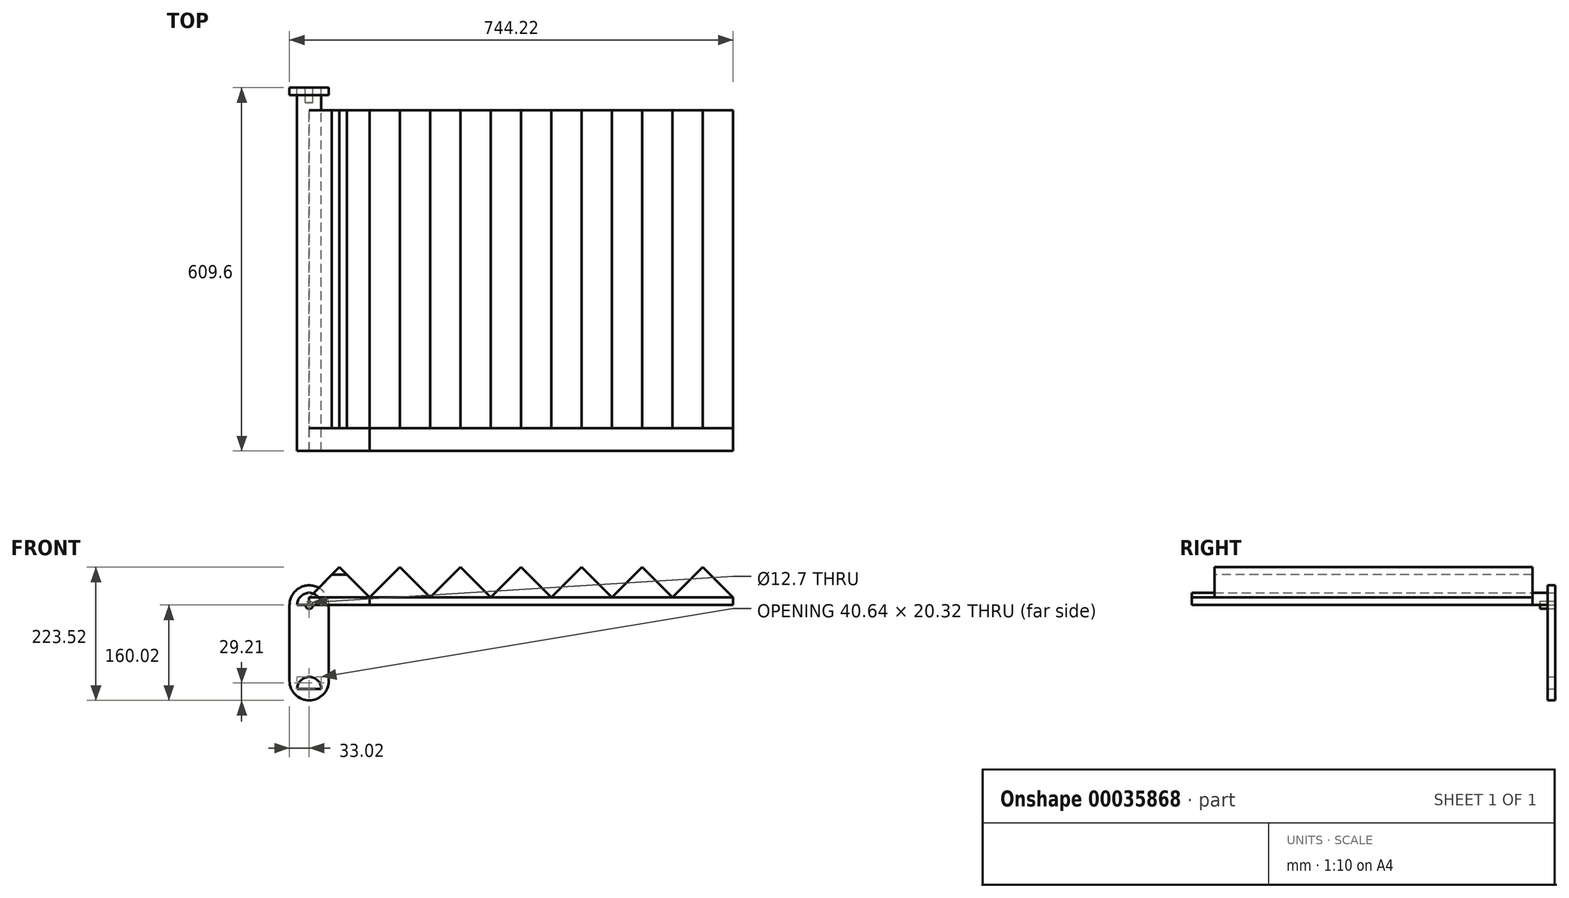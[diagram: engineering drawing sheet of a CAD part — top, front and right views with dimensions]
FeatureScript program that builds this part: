
annotation { "Feature Type Name" : "Feature", "Feature Type Description" : "" }
export const myFeature = defineFeature(function(context is Context, id is Id, definition is map)
    precondition{}
    {
        {
            var Q0;
            Q0=qCreatedBy(makeId("Front.planeOp"),FACE);
            var sketch = newSketch(context, id + "F0", { "sketchPlane" : qUnion([Q0])});
            skLineSegment(sketch, "E0.bottom", {"start": v(0, 0) * mm, "end": v(101.6, 0) * mm});
            skLineSegment(sketch, "E0.top", {"start": v(0, 50.8) * mm, "end": v(101.6, 50.8) * mm});
            skLineSegment(sketch, "E0.left", {"start": v(0, 0) * mm, "end": v(0, 50.8) * mm});
            skLineSegment(sketch, "E0.right", {"start": v(101.6, 0) * mm, "end": v(101.6, 50.8) * mm});
            skSolve(sketch);
        }
        {
            var Q0;
            Q0 = qSketchRegion(id + "F0", true);
            extrude(context, id + "F1", {"entities" : qUnion([Q0]), "depth" : 609.6 * mm});
        }
        {
            var Q0;
            Q0=qCreatedBy(makeId("Front.planeOp"),FACE);
            var sketch = newSketch(context, id + "F2", { "sketchPlane" : qUnion([Q0])});
            skLineSegment(sketch, "E1.bottom", {"start": v(0, 0) * mm, "end": v(711.2, 0) * mm});
            skLineSegment(sketch, "E1.top", {"start": v(0, 63.5) * mm, "end": v(711.2, 63.5) * mm});
            skLineSegment(sketch, "E1.left", {"start": v(0, 0) * mm, "end": v(0, 63.5) * mm});
            skLineSegment(sketch, "E1.right", {"start": v(711.2, 0) * mm, "end": v(711.2, 63.5) * mm});
            skSolve(sketch);
        }
        {
            var Q0;
            Q0 = qSketchRegion(id + "F2", true);
            extrude(context, id + "F3", {"entities" : qUnion([Q0]), "depth" : 609.6 * mm});
        }
        {
            var Q0;
            Q0=makeQuery(id+"F3.opExtrude","CAP_FACE",FACE,{"disambiguationData":[OSD([sQuery(id+"F2.wireOp",EDGE,"E1.bottom"),sQuery(id+"F2.wireOp",EDGE,"E1.top"),sQuery(id+"F2.wireOp",EDGE,"E1.left"),sQuery(id+"F2.wireOp",EDGE,"E1.right")])],"isStart":false});
            var sketch = newSketch(context, id + "F4", { "sketchPlane" : qUnion([Q0])});
            skLineSegment(sketch, "E2", {"start": v(0, 0) * mm, "end": v(0, 12.7) * mm});
            skLineSegment(sketch, "E3", {"start": v(0, 12.7) * mm, "end": v(711.2, 12.7) * mm});
            skLineSegment(sketch, "E4", {"start": v(0, 12.7) * mm, "end": v(101.6, 12.7) * mm});
            skLineSegment(sketch, "E5", {"start": v(50.8, 12.7) * mm, "end": v(50.8, 63.5) * mm});
            skLineSegment(sketch, "E6", {"start": v(50.8, 63.5) * mm, "end": v(0, 12.7) * mm});
            skLineSegment(sketch, "E7", {"start": v(50.8, 63.5) * mm, "end": v(101.6, 12.7) * mm});
            skLineSegment(sketch, "E8.1.0.0", {"start": v(152.4, 63.5) * mm, "end": v(101.6, 12.7) * mm});
            skLineSegment(sketch, "E8.1.0.1", {"start": v(101.6, 12.7) * mm, "end": v(203.2, 12.7) * mm});
            skLineSegment(sketch, "E8.1.0.2", {"start": v(152.4, 12.7) * mm, "end": v(152.4, 63.5) * mm});
            skLineSegment(sketch, "E8.1.0.3", {"start": v(152.4, 63.5) * mm, "end": v(203.2, 12.7) * mm});
            skLineSegment(sketch, "E8.2.0.0", {"start": v(254, 63.5) * mm, "end": v(203.2, 12.7) * mm});
            skLineSegment(sketch, "E8.2.0.1", {"start": v(203.2, 12.7) * mm, "end": v(304.8, 12.7) * mm});
            skLineSegment(sketch, "E8.2.0.2", {"start": v(254, 12.7) * mm, "end": v(254, 63.5) * mm});
            skLineSegment(sketch, "E8.2.0.3", {"start": v(254, 63.5) * mm, "end": v(304.8, 12.7) * mm});
            skLineSegment(sketch, "E8.3.0.0", {"start": v(355.6, 63.5) * mm, "end": v(304.8, 12.7) * mm});
            skLineSegment(sketch, "E8.3.0.1", {"start": v(304.8, 12.7) * mm, "end": v(406.4, 12.7) * mm});
            skLineSegment(sketch, "E8.3.0.2", {"start": v(355.6, 12.7) * mm, "end": v(355.6, 63.5) * mm});
            skLineSegment(sketch, "E8.3.0.3", {"start": v(355.6, 63.5) * mm, "end": v(406.4, 12.7) * mm});
            skLineSegment(sketch, "E8.4.0.0", {"start": v(457.2, 63.5) * mm, "end": v(406.4, 12.7) * mm});
            skLineSegment(sketch, "E8.4.0.1", {"start": v(406.4, 12.7) * mm, "end": v(508, 12.7) * mm});
            skLineSegment(sketch, "E8.4.0.2", {"start": v(457.2, 12.7) * mm, "end": v(457.2, 63.5) * mm});
            skLineSegment(sketch, "E8.4.0.3", {"start": v(457.2, 63.5) * mm, "end": v(508, 12.7) * mm});
            skLineSegment(sketch, "E8.5.0.0", {"start": v(558.8, 63.5) * mm, "end": v(508, 12.7) * mm});
            skLineSegment(sketch, "E8.5.0.1", {"start": v(508, 12.7) * mm, "end": v(609.6, 12.7) * mm});
            skLineSegment(sketch, "E8.5.0.2", {"start": v(558.8, 12.7) * mm, "end": v(558.8, 63.5) * mm});
            skLineSegment(sketch, "E8.5.0.3", {"start": v(558.8, 63.5) * mm, "end": v(609.6, 12.7) * mm});
            skLineSegment(sketch, "E8.6.0.0", {"start": v(660.4, 63.5) * mm, "end": v(609.6, 12.7) * mm});
            skLineSegment(sketch, "E8.6.0.1", {"start": v(609.6, 12.7) * mm, "end": v(711.2, 12.7) * mm});
            skLineSegment(sketch, "E8.6.0.2", {"start": v(660.4, 12.7) * mm, "end": v(660.4, 63.5) * mm});
            skLineSegment(sketch, "E8.6.0.3", {"start": v(660.4, 63.5) * mm, "end": v(711.2, 12.7) * mm});
            skLineSegment(sketch, "E8.direction1", {"start": v(0, 12.7) * mm, "end": v(101.6, 12.7) * mm, "construction": true});
            skSolve(sketch);
        }
        {
            var Q0;
            {var subQ1=sQuery(id+"F4.wireOp",EDGE,"E6");Q0=makeQuery(id+"F4.imprint","IMPRINT",FACE,{"disambiguationData":[TD([[makeQuery(id+"F4.imprint","IMPRINT",EDGE,{"derivedFrom":subQ1}),-1.0]])]});}
            var Q1;
            {var subQ2=sQuery(id+"F4.wireOp",EDGE,"E7");Q1=makeQuery(id+"F4.imprint","IMPRINT",FACE,{"disambiguationData":[TD([[makeQuery(id+"F4.imprint","IMPRINT",EDGE,{"derivedFrom":subQ2}),1.0]])]});}
            var Q2;
            {var subQ2=sQuery(id+"F4.wireOp",EDGE,"E8.1.0.3");Q2=makeQuery(id+"F4.imprint","IMPRINT",FACE,{"disambiguationData":[TD([[makeQuery(id+"F4.imprint","IMPRINT",EDGE,{"derivedFrom":subQ2}),1.0]])]});}
            var Q3;
            {var subQ2=sQuery(id+"F4.wireOp",EDGE,"E8.2.0.3");Q3=makeQuery(id+"F4.imprint","IMPRINT",FACE,{"disambiguationData":[TD([[makeQuery(id+"F4.imprint","IMPRINT",EDGE,{"derivedFrom":subQ2}),1.0]])]});}
            var Q4;
            {var subQ2=sQuery(id+"F4.wireOp",EDGE,"E8.3.0.3");Q4=makeQuery(id+"F4.imprint","IMPRINT",FACE,{"disambiguationData":[TD([[makeQuery(id+"F4.imprint","IMPRINT",EDGE,{"derivedFrom":subQ2}),1.0]])]});}
            var Q5;
            {var subQ2=sQuery(id+"F4.wireOp",EDGE,"E8.4.0.3");Q5=makeQuery(id+"F4.imprint","IMPRINT",FACE,{"disambiguationData":[TD([[makeQuery(id+"F4.imprint","IMPRINT",EDGE,{"derivedFrom":subQ2}),1.0]])]});}
            var Q6;
            {var subQ2=sQuery(id+"F4.wireOp",EDGE,"E8.5.0.3");Q6=makeQuery(id+"F4.imprint","IMPRINT",FACE,{"disambiguationData":[TD([[makeQuery(id+"F4.imprint","IMPRINT",EDGE,{"derivedFrom":subQ2}),1.0]])]});}
            var Q7;
            {var subQ1=sQuery(id+"F4.wireOp",EDGE,"E8.6.0.3");Q7=makeQuery(id+"F4.imprint","IMPRINT",FACE,{"disambiguationData":[TD([[makeQuery(id+"F4.imprint","IMPRINT",EDGE,{"derivedFrom":subQ1}),1.0]])]});}
            extrude(context, id + "F5", {"entities" : qUnion([Q0, Q1, Q2, Q3, Q4, Q5, Q6, Q7]), "operationType" : NewBodyOperationType.REMOVE, "endBound" : BoundingType.THROUGH_ALL, "oppositeDirection" : true, "depth" : 25.4 * mm});
        }
        {
            var Q0;
            Q0=qCreatedBy(makeId("Right.planeOp"),FACE);
            var sketch = newSketch(context, id + "F6", { "sketchPlane" : qUnion([Q0])});
            skLineSegment(sketch, "E9", {"start": v(0, 0) * mm, "end": v(0, 76.2) * mm});
            skLineSegment(sketch, "E10", {"start": v(0, 76.2) * mm, "end": v(-38.1, 76.2) * mm});
            skLineSegment(sketch, "E11", {"start": v(-38.1, 76.2) * mm, "end": v(-38.1, 0) * mm});
            skLineSegment(sketch, "E12", {"start": v(-38.1, 0) * mm, "end": v(0, 0) * mm});
            skLineSegment(sketch, "E13", {"start": v(0, 0) * mm, "end": v(0, 12.7) * mm});
            skLineSegment(sketch, "E14", {"start": v(0, 12.7) * mm, "end": v(-38.1, 12.7) * mm});
            skLineSegment(sketch, "E15", {"start": v(-38.1, 12.7) * mm, "end": v(-38.1, 0) * mm});
            skSolve(sketch);
        }
        {
            var Q0;
            Q0=makeQuery(id+"F6.imprint","IMPRINT",FACE,{"disambiguationData":[TD([[makeQuery(id+"F6.imprint","IMPRINT",EDGE,{"derivedFrom":sQuery(id+"F6.wireOp",EDGE,"E9")}),1.0]])]});
            extrude(context, id + "F7", {"entities" : qUnion([Q0]), "operationType" : NewBodyOperationType.REMOVE, "endBound" : BoundingType.THROUGH_ALL, "depth" : 25.4 * mm});
        }
        {
            var Q0;
            Q0=makeQuery(id+"F3.opExtrude","SWEPT_FACE",FACE,{"disambiguationData":[OSD([sQuery(id+"F2.wireOp",EDGE,"E1.left")])]});
            var sketch = newSketch(context, id + "F8", { "sketchPlane" : qUnion([Q0])});
            skLineSegment(sketch, "E16", {"start": v(609.6, 0) * mm, "end": v(571.5, 0) * mm});
            skLineSegment(sketch, "E17", {"start": v(571.5, 0) * mm, "end": v(571.5, 12.7) * mm});
            skLineSegment(sketch, "E18", {"start": v(571.5, 12.7) * mm, "end": v(609.6, 12.7) * mm});
            skLineSegment(sketch, "E19", {"start": v(609.6, 12.7) * mm, "end": v(609.6, 0) * mm});
            skLineSegment(sketch, "E20", {"start": v(571.5, 12.7) * mm, "end": v(571.5, 88.9) * mm});
            skLineSegment(sketch, "E21", {"start": v(609.6, 12.7) * mm, "end": v(609.6, 88.9) * mm});
            skLineSegment(sketch, "E22", {"start": v(609.6, 88.9) * mm, "end": v(571.5, 88.9) * mm});
            skSolve(sketch);
        }
        {
            var Q0;
            Q0=makeQuery(id+"F8.imprint","IMPRINT",FACE,{"disambiguationData":[TD([[makeQuery(id+"F8.imprint","IMPRINT",EDGE,{"derivedFrom":sQuery(id+"F8.wireOp",EDGE,"E18")}),1.0]])]});
            extrude(context, id + "F9", {"entities" : qUnion([Q0]), "operationType" : NewBodyOperationType.REMOVE, "endBound" : BoundingType.THROUGH_ALL, "oppositeDirection" : true, "depth" : 25.4 * mm});
        }
        {
            var Q0;
            Q0=qCreatedBy(makeId("Front.planeOp"),FACE);
            var sketch = newSketch(context, id + "F10", { "sketchPlane" : qUnion([Q0])});
            skCircle(sketch, "E23", {"center": v(0, 0) * mm, "radius": 6.35 * mm});
            skSolve(sketch);
        }
        {
            var Q0;
            Q0 = qSketchRegion(id + "F10", true);
            extrude(context, id + "F11", {"entities" : qUnion([Q0]), "depth" : 25.4 * mm});
        }
        {
            var Q0;
            Q0=qCreatedBy(makeId("Front.planeOp"),FACE);
            var sketch = newSketch(context, id + "F12", { "sketchPlane" : qUnion([Q0])});
            skArc(sketch, "E24", {"start": v(20.32, 0) * mm, "mid": v(0, 20.32) * mm, "end": v(-20.32, 0) * mm});
            skLineSegment(sketch, "E25", {"start": v(-20.32, 0) * mm, "end": v(20.32, 0) * mm});
            skSolve(sketch);
        }
        {
            var Q0;
            Q0 = qSketchRegion(id + "F12", true);
            extrude(context, id + "F13", {"entities" : qUnion([Q0]), "depth" : 609.6 * mm});
        }
        {
            var Q0;
            Q0=qCreatedBy(makeId("Front.planeOp"),FACE);
            var sketch = newSketch(context, id + "F14", { "sketchPlane" : qUnion([Q0])});
            skArc(sketch, "E26", {"start": v(33.02, 0) * mm, "mid": v(0, 33.02) * mm, "end": v(-33.02, 0) * mm});
            skLineSegment(sketch, "E27", {"start": v(-33.02, 0) * mm, "end": v(-33.02, -127) * mm});
            skLineSegment(sketch, "E28", {"start": v(33.02, 0) * mm, "end": v(33.02, -127) * mm});
            skArc(sketch, "E29", {"start": v(-33.02, -127) * mm, "mid": v(0, -160.02) * mm, "end": v(33.02, -127) * mm});
            skLineSegment(sketch, "E30", {"start": v(0, 33.02) * mm, "end": v(0, 0) * mm});
            skPoint(sketch, "E30.endSnap0", {"position": v(0, 33.02) * mm});
            skCircle(sketch, "E31", {"center": v(0, 0) * mm, "radius": 6.35 * mm});
            skPoint(sketch, "E32.endSnap0", {"position": v(0, -160.02) * mm});
            skLineSegment(sketch, "E33", {"start": v(0, -140.97) * mm, "end": v(-20.32, -140.97) * mm});
            skLineSegment(sketch, "E34", {"start": v(0, -140.97) * mm, "end": v(20.32, -140.97) * mm});
            skPoint(sketch, "E32.start.orphan", {"position": v(0, -160.02) * mm});
            skArc(sketch, "E35.trimOffspring", {"start": v(20.32, -140.97) * mm, "mid": v(0, -120.65) * mm, "end": v(-20.32, -140.97) * mm});
            skSolve(sketch);
        }
        {
            var Q0;
            Q0 = qSketchRegion(id + "F14", true);
            extrude(context, id + "F15", {"entities" : qUnion([Q0]), "depth" : 12.7 * mm});
        }
    });
